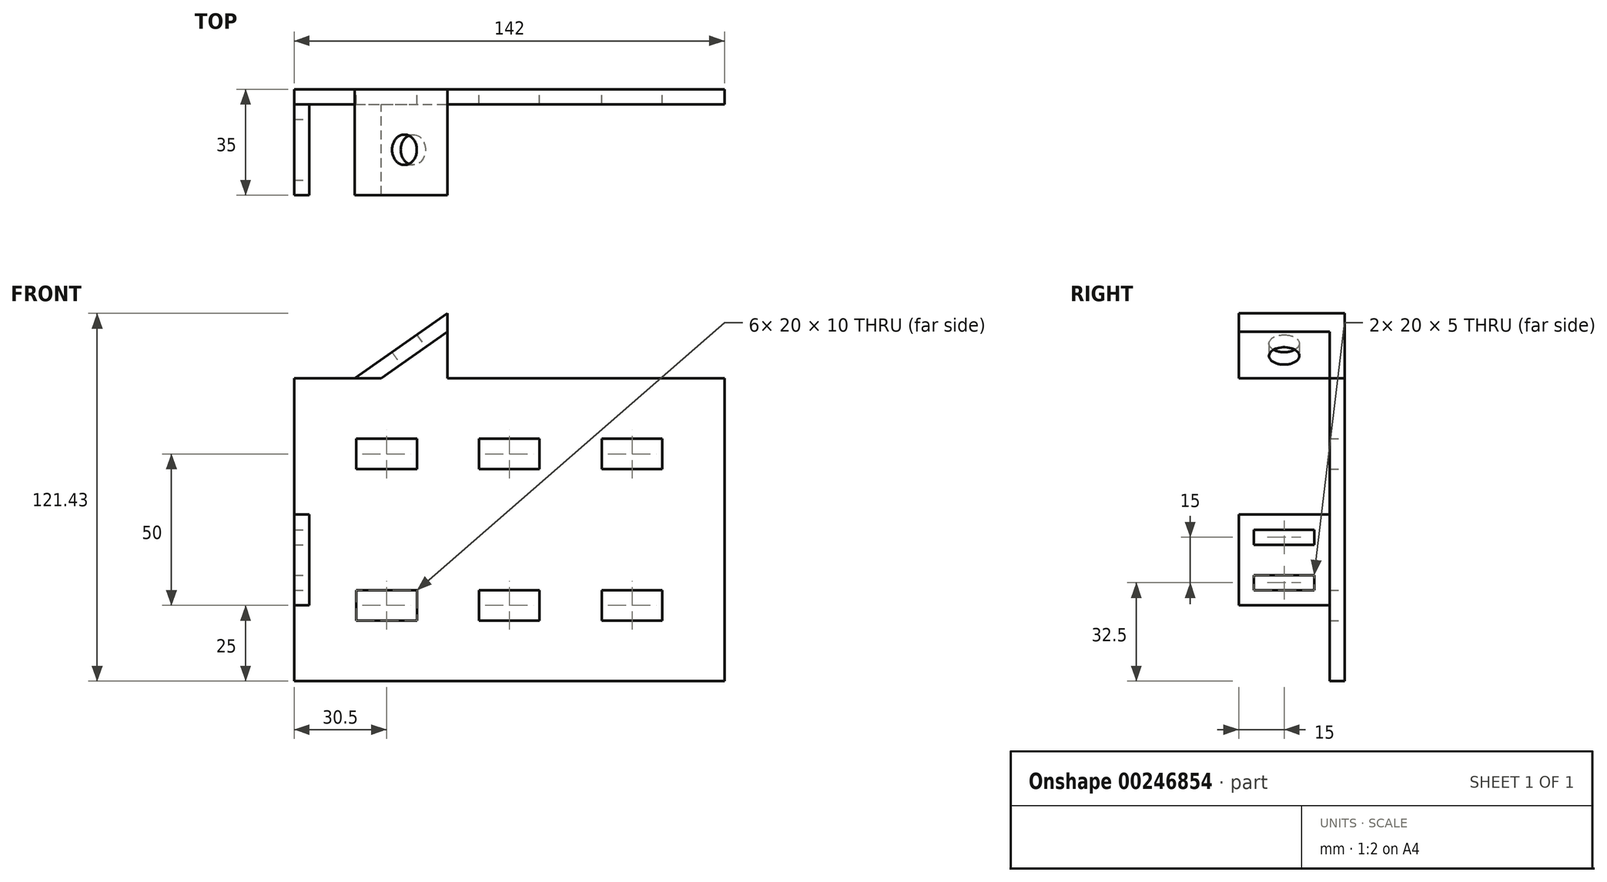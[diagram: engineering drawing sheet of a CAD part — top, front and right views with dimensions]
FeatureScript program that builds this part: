
annotation { "Feature Type Name" : "Feature", "Feature Type Description" : "" }
export const myFeature = defineFeature(function(context is Context, id is Id, definition is map)
    precondition{}
    {
        {
            var Q0;
            Q0=qCreatedBy(makeId("Front.planeOp"),FACE);
            var sketch = newSketch(context, id + "F0", { "sketchPlane" : qUnion([Q0])});
            skLineSegment(sketch, "E0.bottom", {"start": v(0, 0) * mm, "end": v(142, 0) * mm});
            skLineSegment(sketch, "E0.top", {"start": v(0, 100) * mm, "end": v(20, 100) * mm});
            skLineSegment(sketch, "E0.left", {"start": v(0, 0) * mm, "end": v(0, 100) * mm});
            skLineSegment(sketch, "E0.right", {"start": v(142, 0) * mm, "end": v(142, 100) * mm});
            skLineSegment(sketch, "E1.bottom", {"start": v(20.5, 80) * mm, "end": v(40.5, 80) * mm});
            skLineSegment(sketch, "E1.top", {"start": v(20.5, 70) * mm, "end": v(40.5, 70) * mm});
            skLineSegment(sketch, "E1.left", {"start": v(20.5, 80) * mm, "end": v(20.5, 70) * mm});
            skLineSegment(sketch, "E1.right", {"start": v(40.5, 80) * mm, "end": v(40.5, 70) * mm});
            skLineSegment(sketch, "E2.bottom", {"start": v(61, 80) * mm, "end": v(81, 80) * mm});
            skLineSegment(sketch, "E2.top", {"start": v(61, 70) * mm, "end": v(81, 70) * mm});
            skLineSegment(sketch, "E2.left", {"start": v(61, 80) * mm, "end": v(61, 70) * mm});
            skLineSegment(sketch, "E2.right", {"start": v(81, 80) * mm, "end": v(81, 70) * mm});
            skLineSegment(sketch, "E3.bottom", {"start": v(20.5, 30) * mm, "end": v(40.5, 30) * mm});
            skLineSegment(sketch, "E3.top", {"start": v(20.5, 20) * mm, "end": v(40.5, 20) * mm});
            skLineSegment(sketch, "E3.left", {"start": v(20.5, 30) * mm, "end": v(20.5, 20) * mm});
            skLineSegment(sketch, "E3.right", {"start": v(40.5, 30) * mm, "end": v(40.5, 20) * mm});
            skLineSegment(sketch, "E4.bottom", {"start": v(61, 30) * mm, "end": v(81, 30) * mm});
            skLineSegment(sketch, "E4.top", {"start": v(61, 20) * mm, "end": v(81, 20) * mm});
            skLineSegment(sketch, "E4.left", {"start": v(61, 30) * mm, "end": v(61, 20) * mm});
            skLineSegment(sketch, "E4.right", {"start": v(81, 30) * mm, "end": v(81, 20) * mm});
            skLineSegment(sketch, "E5.bottom", {"start": v(101.5, 30) * mm, "end": v(121.5, 30) * mm});
            skLineSegment(sketch, "E5.top", {"start": v(101.5, 20) * mm, "end": v(121.5, 20) * mm});
            skLineSegment(sketch, "E5.left", {"start": v(101.5, 30) * mm, "end": v(101.5, 20) * mm});
            skLineSegment(sketch, "E5.right", {"start": v(121.5, 30) * mm, "end": v(121.5, 20) * mm});
            skLineSegment(sketch, "E6.bottom", {"start": v(101.5, 80) * mm, "end": v(121.5, 80) * mm});
            skLineSegment(sketch, "E6.top", {"start": v(101.5, 70) * mm, "end": v(121.5, 70) * mm});
            skLineSegment(sketch, "E6.left", {"start": v(101.5, 80) * mm, "end": v(101.5, 70) * mm});
            skLineSegment(sketch, "E6.right", {"start": v(121.5, 80) * mm, "end": v(121.5, 70) * mm});
            skLineSegment(sketch, "E7", {"start": v(20, 100) * mm, "end": v(50.6, 121.43) * mm});
            skLineSegment(sketch, "E8", {"start": v(50.6, 121.43) * mm, "end": v(50.6, 100) * mm});
            skLineSegment(sketch, "E9.trimOffspring", {"start": v(50.6, 100) * mm, "end": v(142, 100) * mm});
            skSolve(sketch);
        }
        {
            var Q0;
            Q0 = qSketchRegion(id + "F0", true);
            extrude(context, id + "F1", {"entities" : qUnion([Q0]), "depth" : 5 * mm});
        }
        {
            var Q0;
            Q0=makeQuery(id+"F1.opExtrude","CAP_FACE",FACE,{"disambiguationData":[OSD([sQuery(id+"F0.wireOp",EDGE,"E0.bottom"),sQuery(id+"F0.wireOp",EDGE,"E0.top"),sQuery(id+"F0.wireOp",EDGE,"E0.left"),sQuery(id+"F0.wireOp",EDGE,"E0.right"),sQuery(id+"F0.wireOp",EDGE,"E1.bottom"),sQuery(id+"F0.wireOp",EDGE,"E1.top"),sQuery(id+"F0.wireOp",EDGE,"E1.left"),sQuery(id+"F0.wireOp",EDGE,"E1.right"),sQuery(id+"F0.wireOp",EDGE,"E2.bottom"),sQuery(id+"F0.wireOp",EDGE,"E2.top"),sQuery(id+"F0.wireOp",EDGE,"E2.left"),sQuery(id+"F0.wireOp",EDGE,"E2.right"),sQuery(id+"F0.wireOp",EDGE,"E3.bottom"),sQuery(id+"F0.wireOp",EDGE,"E3.top"),sQuery(id+"F0.wireOp",EDGE,"E3.left"),sQuery(id+"F0.wireOp",EDGE,"E3.right"),sQuery(id+"F0.wireOp",EDGE,"E4.bottom"),sQuery(id+"F0.wireOp",EDGE,"E4.top"),sQuery(id+"F0.wireOp",EDGE,"E4.left"),sQuery(id+"F0.wireOp",EDGE,"E4.right"),sQuery(id+"F0.wireOp",EDGE,"E5.bottom"),sQuery(id+"F0.wireOp",EDGE,"E5.top"),sQuery(id+"F0.wireOp",EDGE,"E5.left"),sQuery(id+"F0.wireOp",EDGE,"E5.right"),sQuery(id+"F0.wireOp",EDGE,"E6.bottom"),sQuery(id+"F0.wireOp",EDGE,"E6.top"),sQuery(id+"F0.wireOp",EDGE,"E6.left"),sQuery(id+"F0.wireOp",EDGE,"E6.right")])],"isStart":false});
            var sketch = newSketch(context, id + "F2", { "sketchPlane" : qUnion([Q0])});
            skLineSegment(sketch, "E10.bottom", {"start": v(0, 25) * mm, "end": v(5, 25) * mm});
            skLineSegment(sketch, "E10.top", {"start": v(0, 55) * mm, "end": v(5, 55) * mm});
            skLineSegment(sketch, "E10.left", {"start": v(0, 25) * mm, "end": v(0, 55) * mm});
            skLineSegment(sketch, "E10.right", {"start": v(5, 25) * mm, "end": v(5, 55) * mm});
            skLineSegment(sketch, "E11", {"start": v(20, 100) * mm, "end": v(28.72, 100) * mm});
            skLineSegment(sketch, "E12", {"start": v(28.72, 100) * mm, "end": v(50.6, 115.33) * mm});
            skLineSegment(sketch, "E13", {"start": v(50.6, 115.33) * mm, "end": v(50.6, 121.43) * mm});
            skLineSegment(sketch, "E14", {"start": v(20, 100) * mm, "end": v(50.6, 121.43) * mm});
            skSolve(sketch);
        }
        {
            var Q0;
            Q0 = qSketchRegion(id + "F2", true);
            extrude(context, id + "F3", {"entities" : qUnion([Q0]), "operationType" : NewBodyOperationType.ADD, "depth" : 30 * mm});
        }
        {
            var Q0;
            Q0=makeQuery(id+"F3.opExtrude","SWEPT_FACE",FACE,{"disambiguationData":[OSD([sQuery(id+"F2.wireOp",EDGE,"E10.right")])]});
            var sketch = newSketch(context, id + "F4", { "sketchPlane" : qUnion([Q0])});
            skLineSegment(sketch, "E15.bottom", {"start": v(-30, 50) * mm, "end": v(-10, 50) * mm});
            skLineSegment(sketch, "E15.top", {"start": v(-30, 45) * mm, "end": v(-10, 45) * mm});
            skLineSegment(sketch, "E15.left", {"start": v(-30, 50) * mm, "end": v(-30, 45) * mm});
            skLineSegment(sketch, "E15.right", {"start": v(-10, 50) * mm, "end": v(-10, 45) * mm});
            skLineSegment(sketch, "E16.bottom", {"start": v(-30, 35) * mm, "end": v(-10, 35) * mm});
            skLineSegment(sketch, "E16.top", {"start": v(-30, 30) * mm, "end": v(-10, 30) * mm});
            skLineSegment(sketch, "E16.left", {"start": v(-30, 35) * mm, "end": v(-30, 30) * mm});
            skLineSegment(sketch, "E16.right", {"start": v(-10, 35) * mm, "end": v(-10, 30) * mm});
            skSolve(sketch);
        }
        {
            var Q0;
            Q0 = qSketchRegion(id + "F4", true);
            var Q1;
            Q1=makeQuery(id+"F3.boolean.opBoolean","MERGE",FACE,{"derivedFrom":[makeQuery(id+"F1.opExtrude","SWEPT_FACE",FACE,{"disambiguationData":[OSD([sQuery(id+"F0.wireOp",EDGE,"E0.left")])]}),makeQuery(id+"F3.opExtrude","SWEPT_FACE",FACE,{"disambiguationData":[OSD([sQuery(id+"F2.wireOp",EDGE,"E10.left")])]})]});
            extrude(context, id + "F5", {"entities" : qUnion([Q0]), "operationType" : NewBodyOperationType.REMOVE, "endBound" : BoundingType.UP_TO_SURFACE, "oppositeDirection" : true, "endBoundEntityFace" : qUnion([Q1]), "depth" : 25 * mm});
        }
        {
            var Q0;
            Q0=makeQuery(id+"F3.opExtrude","SWEPT_FACE",FACE,{"disambiguationData":[OSD([sQuery(id+"F2.wireOp",EDGE,"E12")])]});
            var sketch = newSketch(context, id + "F6", { "sketchPlane" : qUnion([Q0])});
            skCircle(sketch, "E17", {"center": v(93.74, 20) * mm, "radius": 5 * mm});
            skSolve(sketch);
        }
        {
            var Q0;
            Q0 = qSketchRegion(id + "F6", true);
            var Q1;
            Q1=makeQuery(id+"F3.boolean.opBoolean","MERGE",FACE,{"derivedFrom":[makeQuery(id+"F1.opExtrude","SWEPT_FACE",FACE,{"disambiguationData":[OSD([sQuery(id+"F0.wireOp",EDGE,"E7")])]}),makeQuery(id+"F3.opExtrude","SWEPT_FACE",FACE,{"disambiguationData":[OSD([sQuery(id+"F2.wireOp",EDGE,"E14")])]})]});
            extrude(context, id + "F7", {"entities" : qUnion([Q0]), "operationType" : NewBodyOperationType.REMOVE, "endBound" : BoundingType.UP_TO_SURFACE, "oppositeDirection" : true, "endBoundEntityFace" : qUnion([Q1]), "depth" : 25 * mm});
        }
    });
